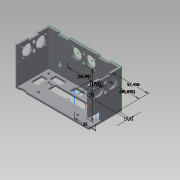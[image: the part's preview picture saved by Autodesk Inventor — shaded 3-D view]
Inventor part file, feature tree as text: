
AUTODESK INVENTOR PART (.ipt)
format: ipt  version: 2015 SP1 (Build 190203100, 203)  size: 478,208 bytes
history: native  units: mm
features: sketch x19, extrude x18, projected_geometry x4, fillet x1, plane x1, chamfer x1
ambient origin geometry x8: Origin, YZ Plane, XZ Plane, XY Plane, X Axis, Y Axis, Z Axis, Center Point
bodies: Body1 (feature_tree)
feature tree (44):
  sketch  "Sketch1"  dims[d49=120.812mm d51=3.0mm]
  extrude  "Extrusion5"  Depth=3.0mm
  extrude  "Extrusion6"  Depth=60.0mm TaperAngle=0.0deg
  extrude  "Extrusion7"  Depth=3.0mm
  extrude  "Extrusion8"  Depth=51.214111mm
  extrude  "Extrusion9"  Depth=10.0mm TaperAngle=0.0deg
  extrude  "Extrusion10"  Depth=17.5mm
  sketch  "Sketch12"  dims[d65=10.0mm d66=17.5mm]
  extrude  "Extrusion11"  Depth=10.0mm TaperAngle=0.0deg
  extrude  "Extrusion12"  Depth=10.0mm TaperAngle=0.0deg
  fillet  "Fillet2"  Radius=22.0mm
  extrude  "Extrusion13"  Depth=15.0mm
  plane  "Work Plane1"
  sketch  "Sketch20"  dims[d80=3.0mm d81=0.0mm d82=10.0mm d83=0.0mm d84=22.0mm]
  extrude  "Extrusion24"  Depth=10.0mm TaperAngle=0.0deg
  extrude  "Extrusion25"  Depth=2.0mm
  extrude  "Extrusion26"  Depth=3.5mm
  extrude  "Extrusion27"  Depth=20.0mm
  extrude  "Extrusion28"  Depth=3.5mm
  extrude  "Extrusion29"  Depth=10.0mm
  extrude  "Extrusion30"  Depth=10.0mm TaperAngle=0.0deg
  chamfer  "Chamfer1"  Distance=10.0mm
  extrude  "Extrusion31"  Depth=10.0mm TaperAngle=0.0deg
  extrude  "Extrusion32"  Depth=7.5mm
  sketch  "Sketch36"  dims[d167=180.0deg d168=7.5mm]
  sketch  "Sketch37"  dims[d169=7.5mm d170=10.0mm d171=0.0mm d172=22.5mm d173=3.0mm d174=22.5mm d175=15.0mm d176=0.0mm d177=7.5mm d178=7.5mm d179=15.0mm d180=0.0mm d187=2.0mm d188=3.0mm d189=6.5mm d190=2.0mm d191=3.0mm d192=6.5mm d193=2.0mm d194=3.0mm d195=2.0mm d196=3.0mm d197=6.5mm d198=6.5mm d199=0.5mm d200=15.0mm d201=0.0mm d202=5.0mm d203=2.0mm d204=45.0deg d223=10.0mm d224=0.0mm d225=17.5mm d226=10.0mm d227=17.5mm d228=6.0mm d229=10.0mm d230=0.0mm d231=3.6mm d232=48.656mm d233=17.5mm d234=57.406mm d235=56.99mm d236=75.0mm d237=35.0mm]
  sketch  "Sketch6"  dims[d52=3.0mm d53=0.0mm d54=60.0mm d55=0.0mm]
  sketch  "Sketch7"  dims[d57=3.0mm d58=3.0mm]
  sketch  "Sketch9"  dims[d59=114.812mm d61=51.214111mm]
  sketch  "Sketch10"  dims[d62=3.5mm d63=10.0mm d64=0.0mm]
  sketch  "Sketch13"  dims[d69=10.0mm d72=10.0mm d73=0.0mm]
  sketch  "Sketch22"  dims[d85=22.0mm d86=15.0mm]
  sketch  "Sketch23"  dims[d87=10.0mm d88=200.0mm d89=0.0mm]
  sketch  "Sketch24"  dims[d90=200.0mm d91=0.0mm d92=2.0mm]
  sketch  "Sketch25"  dims[d95=3.5mm d96=3.5mm]
  sketch  "Sketch26"  dims[d97=3.5mm d99=20.0mm]
  sketch  "Sketch27"  dims[d100=55.0mm d101=3.5mm]
  projected_geometry  "Projected Loop1"
  projected_geometry  "Projected Loop2"
  sketch  "Sketch30"  dims[d102=10.0mm d103=0.0mm d121=19.75mm]
  sketch  "Sketch34"  dims[d132=6.5mm d160=10.0mm d161=0.0mm d162=10.0mm d163=0.0mm]
  projected_geometry  "Projected Loop6"
  sketch  "Sketch35"  dims[d164=17.5mm d165=10.0mm d166=0.0mm]
  projected_geometry  "Projected Loop7"
